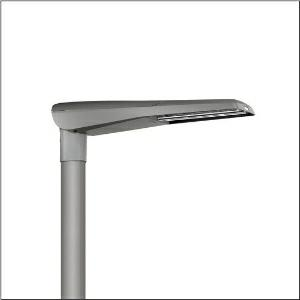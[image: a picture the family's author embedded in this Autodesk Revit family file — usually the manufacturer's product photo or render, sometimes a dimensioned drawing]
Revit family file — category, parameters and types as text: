
# Revit family: streetlight_sl_11_iq_mini___st1_0a_5xc2mc1f08he_59d2
name_source: partatom
category: Lighting Fixtures
units: mm (PartAtom-declared; Revit-internal decimal feet)

## family parameters
Cut with Voids When Loaded = No
Host = Face
Light Source = No
Part Type = Normal
Room Calculation Point = No
Round Connector Dimension = Use Diameter
Shared = No

## types (1)
- --- (1 x LED, 6610 lm, 63.6 W, 2200K)
    Apparent Load = 64 VA
    CIE Flux Codes = 33 66 96 100 100
    Color Rendering = 70
    Color Temperature = 2200K
    Default Elevation = 1800 mm
    Description = Streetlight SL 11 iQ mini, mast luminaire, primary light control with 3 zone facetted reflector, of plastic, silver coated, highly specular, primary optical cover: cover, of PMMA, transparent, light distribution: ST1.0a, light emission: direct distribution, primary light characteristic: asymmetric, installation type: post-top, side-entry, lamps: LED, High Power LED, rated values: 8.070lm | 62,2W | 129,7lm/W (begin service life); end service life: 8.070lm | 65,6W; at 50% lumin. flux: 4.035lm | 29,4W | 137,2lm/W, colour temperature: 2200/2700/3000/4000K, colour rendering: CRI > 70, light colour: 722/727/730/740, light setting 1 begin service life: 100% | 8.070lm | 62,2W | 129,7lm/W | 3.000K, light setting 1 end service life: 65,6W, further light settings possible, control: Street-Remote, Auto-Match, Temp-Guard, Lumen-Switch, Night-Set, Smart-Wire, Light-Fading, Desk-Remote (wireless, voltage-free reading and setting of iQ features in the workshop via application-optimized NFC function/RFID function), optimised constant luminous flux control (CLO 2.0), with cable H07RN-F 5x 1.5mm², mains connection: 230..240V, AC, 50/60Hz, connection cable pre-assembled, cable length: 8,5m, luminaire housing, of diecast aluminium, powder-coated, Siteco® metallic grey (DB 702S), please order mast flange separately, inclination adjustable without tools: 0°, 5°, 10°, 15° (post-top) | 0°, -5°, -10°, -15° (side-entry), sealing non-destructively replaceable, multi-level sealing system, length: 736mm, width: 174mm, height: 116mm, mast flange for spigot size: 42mm (side-entry): 5XC10008XM4, 60/48mm (side-entry/post-top): 5XC10108XM2, 76/60mm (side-entry/post-top): 5XC10108XM1, equipment: Power, protection rating (complete): IP66, insulation class (complete): insulation class II (safety insulation), certification: CE, ENEC, ENEC+, VDE, impact resistance: IK10, permissible operating ambient temperature for outdoor applications: -25..+50°C, standard-compliant lighting for roads and squares, Environmental Product Declaration (EPD) tested and certified by an independent institute, packaging unit: 1 piece

Light Distribution: ST1.0a
    Height = 116 mm
    Lamp = 1 x LED
    Lamp Light Flux = 6610 lm
    Lamp Power = 63.6 W
    Lamp count = 1
    Length = 736 mm
    Luminous efficacy = 104 lm/W
    Manufacturer = Siteco
    ModVariant = No
    Model = 5XC2MC1F08HE
    Number of Poles = 1
    OnlyDefault = Yes
    Power Factor = 1
    Product Name = Streetlight SL 11 iQ mini | ST1.0a
    Product group = mast luminaire | pylon top
    ProductGroupID = 6100
    Protection Class = Protection class II
    Protection Degree = IP 66
    RLX_Detail_Level = 1
    RLX_Emergency_Light_Flux = 0 lm
    RLX_Emergency_Type = 0
    RLX_Emergency_Type_DB = No
    RlxData = <blob elided: 53261 chars, md5=fa002257>
    Socket = socket
    Standby Power = 0 W
    System Light Flux = 6610 lm
    System Power = 64 W
    Type Comments = individual setting: luminous flux: 100 % | dim-lin: 254 | 866 mA
    Type Image = l_1003508.jpg
    URL = http://relux.com
    VarID = @adj_055735
    Voltage = 0 V
    Weight = 0.00 kg
    Width = 174 mm

## geometry (parser evidence)
native form markers: Blend x4, Sweep x10
no freeform markers — native parametric forms only
